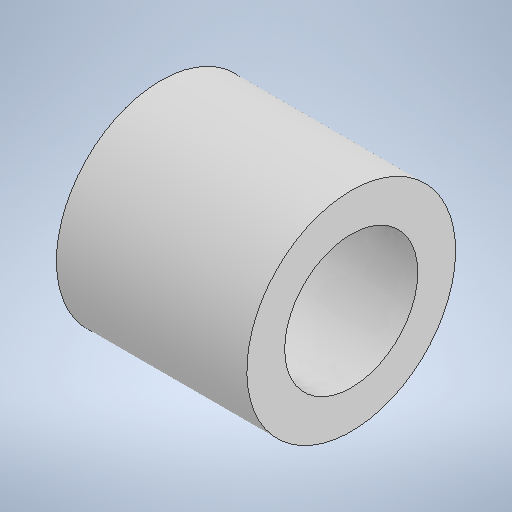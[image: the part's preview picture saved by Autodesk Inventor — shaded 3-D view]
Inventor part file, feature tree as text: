
AUTODESK INVENTOR PART (.ipt)
format: ipt  version: 2025.1 (Build 291241020, 241B)  size: 218,112 bytes
history: native  units: in
note: dims shown in document units (in); Inventor stores cm internally (conversion verified against a paired STEP export)
features: extrude x1, sketch x1
ambient origin geometry x8: Origin, YZ Plane, XZ Plane, XY Plane, X Axis, Y Axis, Z Axis, Center Point
bodies: Solid1 (feature_tree)
feature tree (2):
  extrude  "Extrusion1"  Depth=0.73in
  sketch  "Sketch1"  dims[d0=0.51in d1=0.8in d2=0.73in d3=0.0in]
